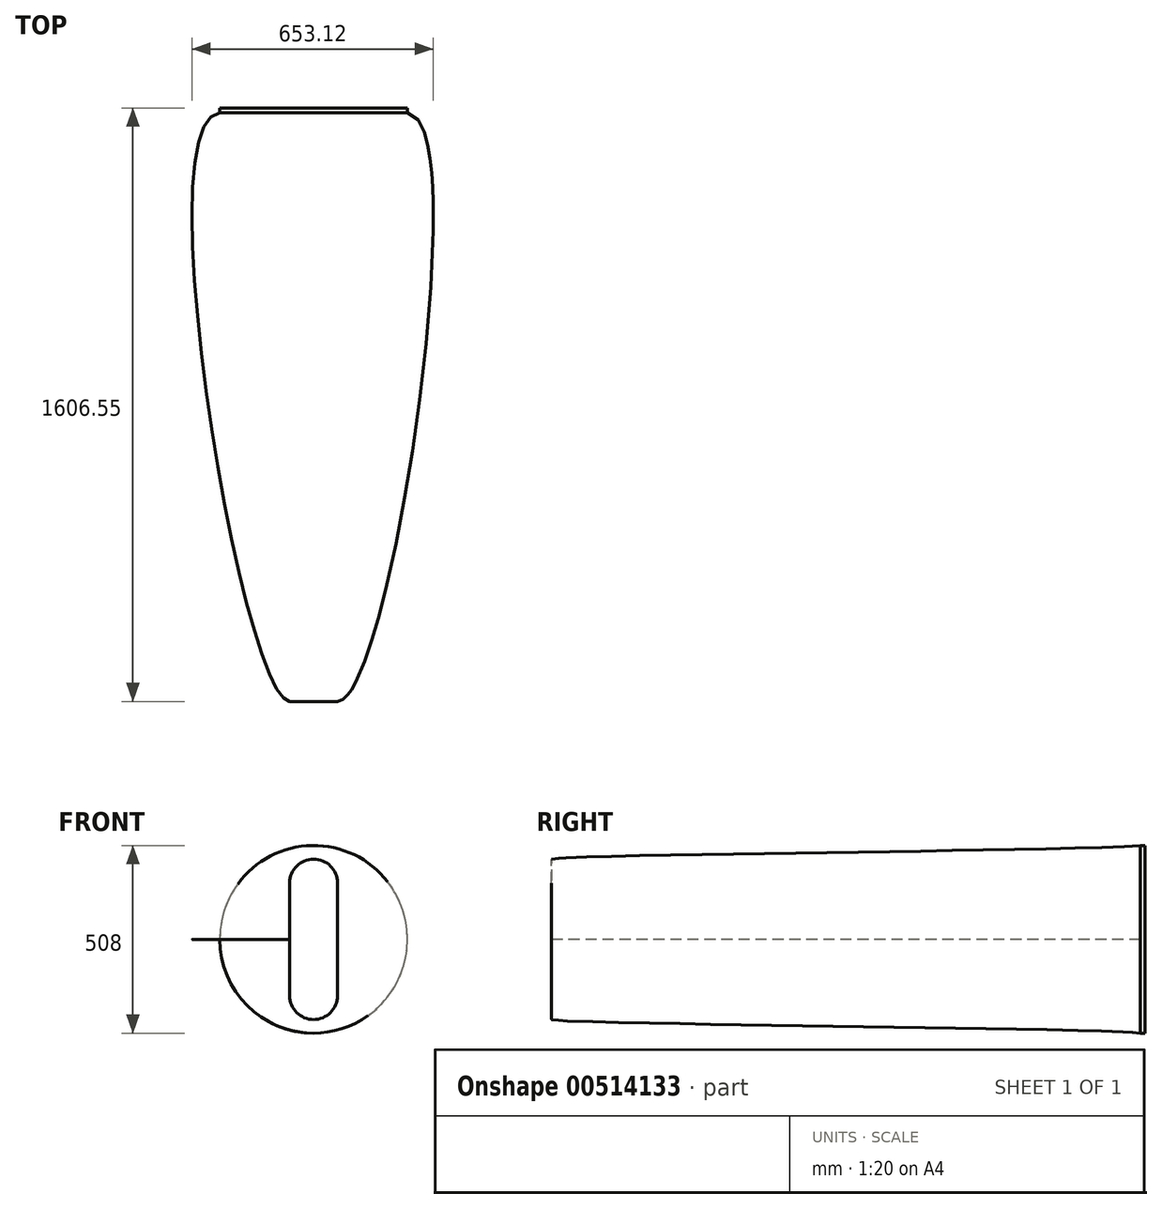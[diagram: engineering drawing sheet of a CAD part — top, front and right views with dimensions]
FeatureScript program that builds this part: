
annotation { "Feature Type Name" : "Feature", "Feature Type Description" : "" }
export const myFeature = defineFeature(function(context is Context, id is Id, definition is map)
    precondition{}
    {
        {
            var Q0;
            Q0=qCreatedBy(makeId("Front.planeOp"),FACE);
            var sketch = newSketch(context, id + "F0", { "sketchPlane" : qUnion([Q0])});
            skCircle(sketch, "E0", {"center": v(0, 0) * mm, "radius": 254 * mm});
            skSolve(sketch);
        }
        {
            var Q0;
            Q0=qCreatedBy(makeId("Front.planeOp"),FACE);
            cPlane(context, id + "F1", {"entities" : qUnion([Q0]), "cplaneType" : CPlaneType.OFFSET, "offset" : 1600.2 * mm, "width" : 152.4 * mm, "height" : 152.4 * mm});
        }
        {
            var Q0;
            Q0=qCreatedBy(id+"F1.planeOp",FACE);
            var sketch = newSketch(context, id + "F2", { "sketchPlane" : qUnion([Q0])});
            skLineSegment(sketch, "E1.bottom", {"start": v(-64.82, 152.4) * mm, "end": v(64.82, 152.4) * mm});
            skLineSegment(sketch, "E1.top", {"start": v(-64.82, -152.4) * mm, "end": v(64.82, -152.4) * mm});
            skLineSegment(sketch, "E1.left", {"start": v(-64.82, 152.4) * mm, "end": v(-64.82, -152.4) * mm});
            skLineSegment(sketch, "E1.right", {"start": v(64.82, 152.4) * mm, "end": v(64.82, -152.4) * mm});
            skPoint(sketch, "E1.middle", {"position": v(0, 0) * mm});
            skArc(sketch, "E2", {"start": v(64.82, 152.4) * mm, "mid": v(0, 217.22) * mm, "end": v(-64.82, 152.4) * mm});
            skArc(sketch, "E3", {"start": v(-64.82, -152.4) * mm, "mid": v(0, -217.22) * mm, "end": v(64.82, -152.4) * mm});
            skSolve(sketch);
        }
        {
            var Q0;
            Q0=makeQuery(id+"F0.imprint","IMPRINT",FACE,{"disambiguationData":[TD([[makeQuery(id+"F0.imprint","IMPRINT",EDGE,{"derivedFrom":sQuery(id+"F0.wireOp",EDGE,"E0")}),1.0]])]});
            extrude(context, id + "F3", {"entities" : qUnion([Q0]), "endBound" : BoundingType.SYMMETRIC, "depth" : 12.7 * mm});
        }
        {
            var Q0;
            Q0=makeQuery(id+"F3.opExtrude","CAP_FACE",FACE,{"disambiguationData":[OSD([sQuery(id+"F0.wireOp",EDGE,"E0")])],"isStart":false});
            var sketch = newSketch(context, id + "F4", { "sketchPlane" : qUnion([Q0])});
            skPoint(sketch, "E4", {"position": v(0, 254) * mm});
            skPoint(sketch, "E5", {"position": v(254, 0) * mm});
            skPoint(sketch, "E6", {"position": v(-254, 0) * mm});
            skPoint(sketch, "E7", {"position": v(0, -254) * mm});
            skSolve(sketch);
        }
        {
            var Q0;
            Q0=makeQuery(id+"F4.imprint","IMPRINT",FACE,{"disambiguationData":[TD([[makeQuery(id+"F4.imprint","IMPRINT",EDGE,{"derivedFrom":makeQuery(id+"F3.opExtrude","CAP_EDGE",EDGE,{"disambiguationData":[OSD([sQuery(id+"F0.wireOp",EDGE,"E0")])],"isStart":false})}),1.0]])]});
            var sketch = newSketch(context, id + "F5", { "sketchPlane" : qUnion([Q0])});
            skArc(sketch, "E8", {"start": v(-205.1, 149.82) * mm, "mid": v(-250.76, -40.41) * mm, "end": v(-147.66, -206.67) * mm});
            skArc(sketch, "E9", {"start": v(200.4, 156.06) * mm, "mid": v(-3.9, 253.97) * mm, "end": v(-205.1, 149.82) * mm});
            skArc(sketch, "E10", {"start": v(147.41, -206.84) * mm, "mid": v(251.33, -36.7) * mm, "end": v(200.4, 156.06) * mm});
            skArc(sketch, "E11", {"start": v(-147.66, -206.67) * mm, "mid": v(-0.15, -254) * mm, "end": v(147.41, -206.84) * mm});
            skSolve(sketch);
        }
        {
            var Q0;
            Q0=qCreatedBy(makeId("Top.planeOp"),FACE);
            var sketch = newSketch(context, id + "F6", { "sketchPlane" : qUnion([Q0])});
            skFitSpline(sketch, "E12", {"points": [v(64.82, -1600.2) * mm, v(254, -6.35) * mm], "startDerivative": vector(428.08, 3.34) * mm, "endDerivative": vector(-564.96, 56.87) * mm});
            skFitSpline(sketch, "E13", {"points": [v(-64.82, -1600.2) * mm, v(-254, -6.35) * mm], "startDerivative": vector(-375.4, 10.29) * mm, "endDerivative": vector(617.33, 71.98) * mm});
            skSolve(sketch);
        }
        {
            var Q1;
            Q1 = qSketchRegion(id + "F5", true);
            var Q2;
            Q2 = qSketchRegion(id + "F2", true);
            var Q3;
            Q3=sQuery(id+"F6.wireOp",EDGE,"E13");
            var Q4;
            Q4=sQuery(id+"F6.wireOp",EDGE,"E12");
            loft(context, id + "F7", {"addGuides" : true, "sheetProfilesArray" : [{ "sheetProfileEntities" : qUnion([Q1]) }, { "sheetProfileEntities" : qUnion([Q2]) }], "guidesArray" : [{ "guideEntities" : qUnion([Q3]), "guideDerivativeType" : LoftGuideDerivativeType.DEFAULT, "guideDerivativeMagnitude" : 1 }, { "guideEntities" : qUnion([Q4]), "guideDerivativeType" : LoftGuideDerivativeType.DEFAULT, "guideDerivativeMagnitude" : 1 }]});
        }
    });
